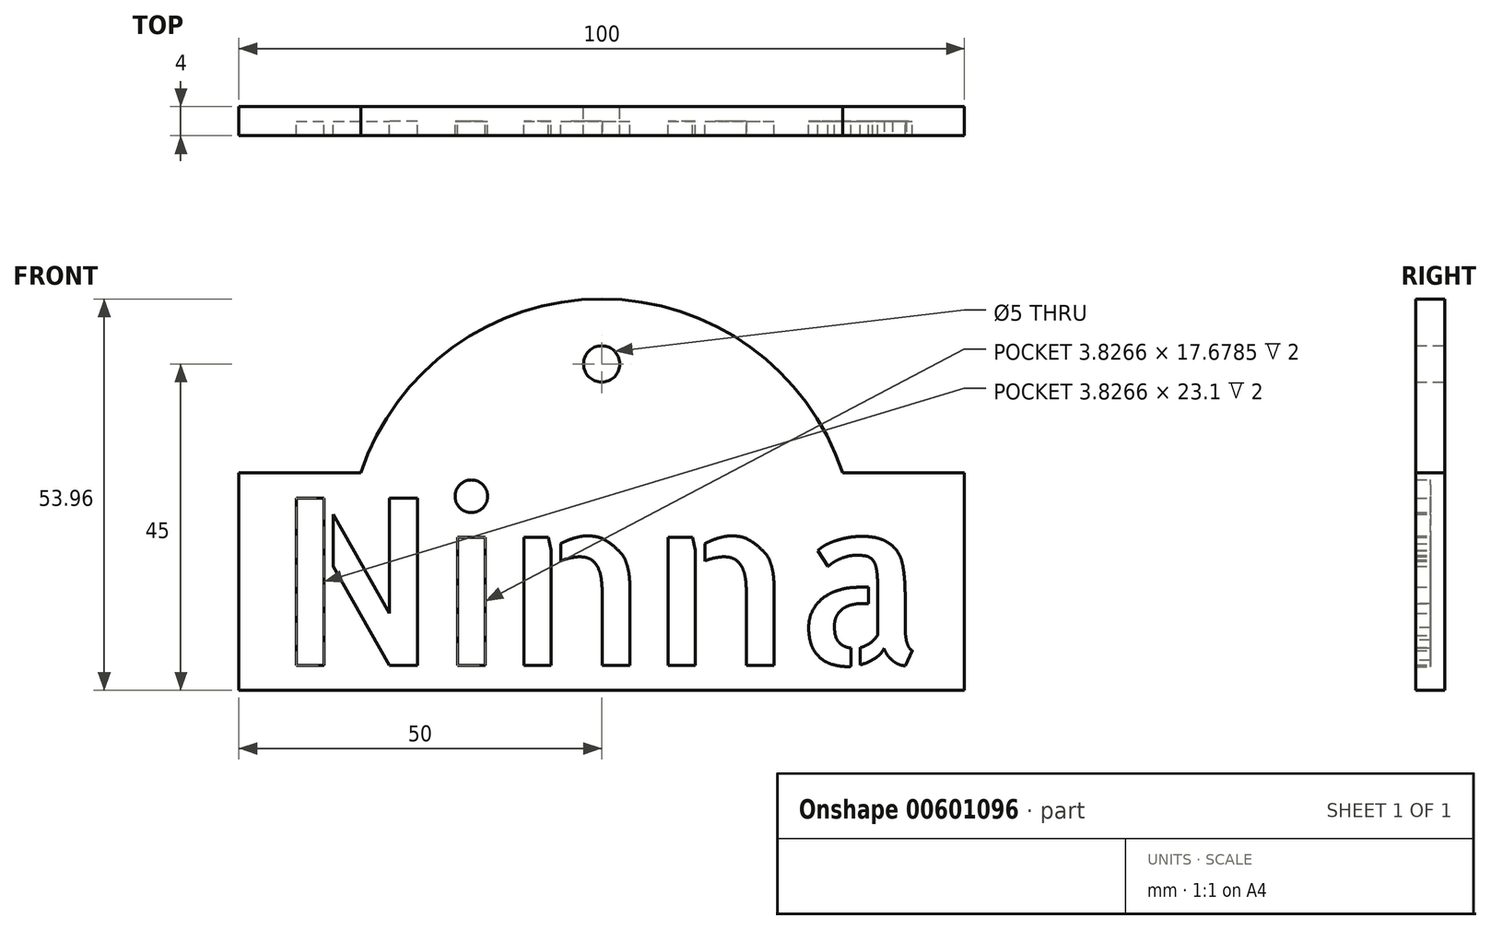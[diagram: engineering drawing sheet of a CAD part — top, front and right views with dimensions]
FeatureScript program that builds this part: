
annotation { "Feature Type Name" : "Feature", "Feature Type Description" : "" }
export const myFeature = defineFeature(function(context is Context, id is Id, definition is map)
    precondition{}
    {
        {
            var Q0;
            Q0=qCreatedBy(makeId("Front.planeOp"),FACE);
            var sketch = newSketch(context, id + "F0", { "sketchPlane" : qUnion([Q0])});
            skLineSegment(sketch, "E0.bottom", {"start": v(-50, 45.57) * mm, "end": v(-33.21, 45.57) * mm});
            skLineSegment(sketch, "E0.top", {"start": v(-50, 15.57) * mm, "end": v(50, 15.57) * mm});
            skLineSegment(sketch, "E0.left", {"start": v(-50, 45.57) * mm, "end": v(-50, 15.57) * mm});
            skLineSegment(sketch, "E0.right", {"start": v(50, 45.57) * mm, "end": v(50, 15.57) * mm});
            skArc(sketch, "E1", {"start": v(33.21, 45.57) * mm, "mid": v(0, 69.53) * mm, "end": v(-33.21, 45.57) * mm});
            skPoint(sketch, "E2", {"position": v(-50, 30.57) * mm});
            skPoint(sketch, "E3", {"position": v(0, 15.57) * mm});
            skCircle(sketch, "E4", {"center": v(0, 60.57) * mm, "radius": 2.5 * mm});
            skPoint(sketch, "E5", {"position": v(0, 69.53) * mm});
            skPoint(sketch, "E6", {"position": v(0, 45.57) * mm});
            skText(sketch, "E7", { "text": "Ninna", "fontName": "AllertaStencil-Regular.ttf"});
            skPoint(sketch, "E8", {"position": v(-45, 30.57) * mm});
            skPoint(sketch, "E9", {"position": v(0, 19.01) * mm});
            skLineSegment(sketch, "E10.trimOffspring", {"start": v(33.21, 45.57) * mm, "end": v(50, 45.57) * mm});
            const initialGuessF0  = {"E7": [-0.045, 0.01901, 1, 0, 0.02311]};
            skSetInitialGuess(sketch, initialGuessF0);
            skSolve(sketch);
        }
        {
            var Q0;
            Q0 = qSketchRegion(id + "F0", true);
            var Q1;
            Q1=makeQuery(id+"F0.imprint","IMPRINT",FACE,{"disambiguationData":[TD([[makeQuery(id+"F0.imprint","IMPRINT",EDGE,{"derivedFrom":sQuery(id+"F0.wireOp",EDGE,"E7.sketch_text.stroke-0")}),-1.0]])]});
            var Q2;
            Q2=makeQuery(id+"F0.imprint","IMPRINT",FACE,{"disambiguationData":[TD([[makeQuery(id+"F0.imprint","IMPRINT",EDGE,{"derivedFrom":sQuery(id+"F0.wireOp",EDGE,"E7.sketch_text.stroke-7")}),-1.0]])]});
            var Q3;
            Q3=makeQuery(id+"F0.imprint","IMPRINT",FACE,{"disambiguationData":[TD([[makeQuery(id+"F0.imprint","IMPRINT",EDGE,{"derivedFrom":sQuery(id+"F0.wireOp",EDGE,"E7.sketch_text.stroke-11")}),-1.0]])]});
            var Q4;
            Q4=makeQuery(id+"F0.imprint","IMPRINT",FACE,{"disambiguationData":[TD([[makeQuery(id+"F0.imprint","IMPRINT",EDGE,{"derivedFrom":sQuery(id+"F0.wireOp",EDGE,"E7.sketch_text.stroke-15")}),-1.0]])]});
            var Q5;
            Q5=makeQuery(id+"F0.imprint","IMPRINT",FACE,{"disambiguationData":[TD([[makeQuery(id+"F0.imprint","IMPRINT",EDGE,{"derivedFrom":sQuery(id+"F0.wireOp",EDGE,"E7.sketch_text.stroke-23")}),-1.0]])]});
            var Q6;
            Q6=makeQuery(id+"F0.imprint","IMPRINT",FACE,{"disambiguationData":[TD([[makeQuery(id+"F0.imprint","IMPRINT",EDGE,{"derivedFrom":sQuery(id+"F0.wireOp",EDGE,"E7.sketch_text.stroke-28")}),-1.0]])]});
            var Q7;
            Q7=makeQuery(id+"F0.imprint","IMPRINT",FACE,{"disambiguationData":[TD([[makeQuery(id+"F0.imprint","IMPRINT",EDGE,{"derivedFrom":sQuery(id+"F0.wireOp",EDGE,"E7.sketch_text.stroke-47")}),-1.0]])]});
            var Q8;
            Q8=makeQuery(id+"F0.imprint","IMPRINT",FACE,{"disambiguationData":[TD([[makeQuery(id+"F0.imprint","IMPRINT",EDGE,{"derivedFrom":sQuery(id+"F0.wireOp",EDGE,"E7.sketch_text.stroke-52")}),-1.0]])]});
            var Q9;
            Q9=makeQuery(id+"F0.imprint","IMPRINT",FACE,{"disambiguationData":[TD([[makeQuery(id+"F0.imprint","IMPRINT",EDGE,{"derivedFrom":sQuery(id+"F0.wireOp",EDGE,"E7.sketch_text.stroke-71")}),-1.0]])]});
            var Q10;
            Q10=makeQuery(id+"F0.imprint","IMPRINT",FACE,{"disambiguationData":[TD([[makeQuery(id+"F0.imprint","IMPRINT",EDGE,{"derivedFrom":sQuery(id+"F0.wireOp",EDGE,"E7.sketch_text.stroke-90")}),-1.0]])]});
            var Q11;
            Q11=makeQuery(id+"F0.imprint","IMPRINT",FACE,{"disambiguationData":[TD([[makeQuery(id+"F0.imprint","IMPRINT",EDGE,{"derivedFrom":sQuery(id+"F0.wireOp",EDGE,"E0.bottom")}),-1.0]])]});
            extrude(context, id + "F1", {"entities" : qUnion([Q0, Q1, Q2, Q3, Q4, Q5, Q6, Q7, Q8, Q9, Q10, Q11]), "depth" : 2 * mm, "offsetDistance" : 25 * mm});
        }
        {
            var Q0;
            Q0=makeQuery(id+"F0.imprint","IMPRINT",FACE,{"disambiguationData":[TD([[makeQuery(id+"F0.imprint","IMPRINT",EDGE,{"derivedFrom":sQuery(id+"F0.wireOp",EDGE,"E0.bottom")}),-1.0]])]});
            extrude(context, id + "F2", {"entities" : qUnion([Q0]), "operationType" : NewBodyOperationType.ADD, "depth" : 4 * mm, "offsetDistance" : 25 * mm});
        }
    });
